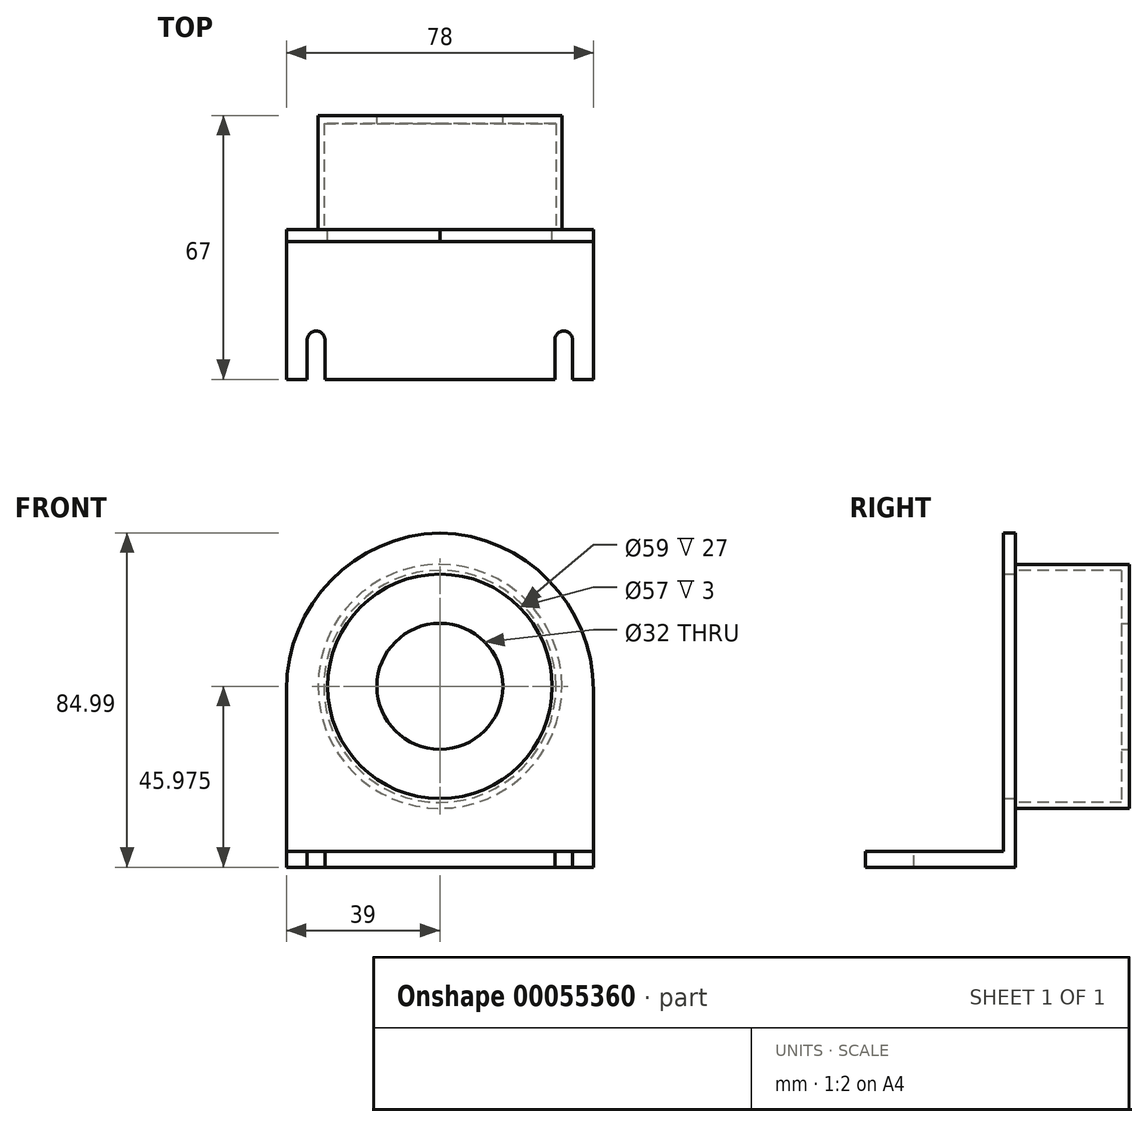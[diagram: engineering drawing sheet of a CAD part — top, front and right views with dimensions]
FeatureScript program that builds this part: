
annotation { "Feature Type Name" : "Feature", "Feature Type Description" : "" }
export const myFeature = defineFeature(function(context is Context, id is Id, definition is map)
    precondition{}
    {
        {
            var Q0;
            Q0=qCreatedBy(makeId("Top.planeOp"),FACE);
            var sketch = newSketch(context, id + "F0", { "sketchPlane" : qUnion([Q0])});
            skLineSegment(sketch, "E0.rect.bottom", {"start": v(39, 19) * mm, "end": v(-39, 19) * mm});
            skLineSegment(sketch, "E0.rect.top", {"start": v(39, -19) * mm, "end": v(-39, -19) * mm});
            skLineSegment(sketch, "E0.rect.left", {"start": v(39, 19) * mm, "end": v(39, -19) * mm});
            skLineSegment(sketch, "E0.rect.right", {"start": v(-39, 19) * mm, "end": v(-39, -19) * mm});
            skPoint(sketch, "E0.rect.middle", {"position": v(0, 0) * mm});
            skSolve(sketch);
        }
        {
            var Q0;
            Q0=qSketchRegion(id+"F0",true);
            extrude(context, id + "F1", {"entities" : qUnion([Q0]), "depth" : 4 * mm});
        }
        {
            var Q0;
            Q0=makeQuery(id+"F1.opExtrude","CAP_FACE",FACE,{"disambiguationData":[OSD([sQuery(id+"F0.wireOp",EDGE,"E0.rect.bottom"),sQuery(id+"F0.wireOp",EDGE,"E0.rect.top"),sQuery(id+"F0.wireOp",EDGE,"E0.rect.left"),sQuery(id+"F0.wireOp",EDGE,"E0.rect.right")])],"isStart":false});
            var sketch = newSketch(context, id + "F2", { "sketchPlane" : qUnion([Q0])});
            skLineSegment(sketch, "E1.bottom", {"start": v(-39, 19) * mm, "end": v(39, 19) * mm});
            skLineSegment(sketch, "E1.top", {"start": v(-39, 16) * mm, "end": v(39, 16) * mm});
            skLineSegment(sketch, "E1.left", {"start": v(-39, 19) * mm, "end": v(-39, 16) * mm});
            skLineSegment(sketch, "E1.right", {"start": v(39, 19) * mm, "end": v(39, 16) * mm});
            skSolve(sketch);
        }
        {
            var Q0;
            Q0=qSketchRegion(id+"F2",true);
            extrude(context, id + "F3", {"entities" : qUnion([Q0]), "operationType" : NewBodyOperationType.ADD, "depth" : 81 * mm});
        }
        {
            var Q0;
            Q0=makeQuery(id+"F3.opExtrude","CAP_EDGE",EDGE,{"disambiguationData":[OSD([sQuery(id+"F2.wireOp",EDGE,"E1.right")])],"isStart":false});
            var Q1;
            Q1=makeQuery(id+"F3.opExtrude","CAP_EDGE",EDGE,{"disambiguationData":[OSD([sQuery(id+"F2.wireOp",EDGE,"E1.left")])],"isStart":false});
            fillet(context, id + "F4", {"entities" : qUnion([Q0, Q1]), "radius" : 40 * mm, "tangentPropagation" : true, "allowEdgeOverflow" : false});
        }
        {
            var Q0;
            Q0=makeQuery(id+"F3.boolean.opBoolean","MERGE",FACE,{"derivedFrom":[makeQuery(id+"F1.opExtrude","SWEPT_FACE",FACE,{"disambiguationData":[OSD([sQuery(id+"F0.wireOp",EDGE,"E0.rect.bottom")])]}),makeQuery(id+"F3.opExtrude","SWEPT_FACE",FACE,{"disambiguationData":[OSD([sQuery(id+"F2.wireOp",EDGE,"E1.bottom")])]})]});
            var sketch = newSketch(context, id + "F5", { "sketchPlane" : qUnion([Q0])});
            skPoint(sketch, "E2.first.point", {"position": v(0, 84.99) * mm});
            skPoint(sketch, "E2.second.point", {"position": v(39, 45) * mm});
            skPoint(sketch, "E2.third.point", {"position": v(-39, 45) * mm});
            skCircle(sketch, "E3", {"center": v(0, 45.98) * mm, "radius": 31 * mm});
            skCircle(sketch, "E4", {"center": v(0, 45.98) * mm, "radius": 29.5 * mm});
            skSolve(sketch);
        }
        {
            var Q0;
            Q0=qSketchRegion(id+"F5",true);
            extrude(context, id + "F6", {"entities" : qUnion([Q0]), "operationType" : NewBodyOperationType.ADD, "depth" : 27 * mm});
        }
        {
            var Q0;
            Q0=makeQuery(id+"F6.boolean.opBoolean","SPLIT",FACE,{"disambiguationData":[TD([makeQuery(id+"F6.opExtrude","SWEPT_FACE",FACE,{"disambiguationData":[OSD([sQuery(id+"F5.wireOp",EDGE,"E4")])]})])],"derivedFrom":makeQuery(id+"F3.boolean.opBoolean","MERGE",FACE,{"derivedFrom":[makeQuery(id+"F1.opExtrude","SWEPT_FACE",FACE,{"disambiguationData":[OSD([sQuery(id+"F0.wireOp",EDGE,"E0.rect.bottom")])]}),makeQuery(id+"F3.opExtrude","SWEPT_FACE",FACE,{"disambiguationData":[OSD([sQuery(id+"F2.wireOp",EDGE,"E1.bottom")])]})]})});
            var sketch = newSketch(context, id + "F7", { "sketchPlane" : qUnion([Q0])});
            skCircle(sketch, "E5", {"center": v(0, 45.98) * mm, "radius": 28.5 * mm});
            skSolve(sketch);
        }
        {
            var Q0;
            Q0=qSketchRegion(id+"F7",true);
            extrude(context, id + "F8", {"entities" : qUnion([Q0]), "operationType" : NewBodyOperationType.REMOVE, "endBound" : BoundingType.UP_TO_NEXT, "oppositeDirection" : true, "depth" : 25 * mm});
        }
        {
            var Q0;
            Q0=makeQuery(id+"F6.opExtrude","CAP_FACE",FACE,{"disambiguationData":[OSD([sQuery(id+"F5.wireOp",EDGE,"E3"),sQuery(id+"F5.wireOp",EDGE,"E4")])],"isStart":false});
            var sketch = newSketch(context, id + "F9", { "sketchPlane" : qUnion([Q0])});
            skCircle(sketch, "E6", {"center": v(0, 45.98) * mm, "radius": 31 * mm});
            skSolve(sketch);
        }
        {
            var Q0;
            Q0=qSketchRegion(id+"F9",true);
            extrude(context, id + "F10", {"entities" : qUnion([Q0]), "operationType" : NewBodyOperationType.ADD, "depth" : 2 * mm});
        }
        {
            var Q0;
            Q0=makeQuery(id+"F10.opExtrude","CAP_FACE",FACE,{"disambiguationData":[OSD([sQuery(id+"F9.wireOp",EDGE,"E6")])],"isStart":false});
            var sketch = newSketch(context, id + "F11", { "sketchPlane" : qUnion([Q0])});
            skCircle(sketch, "E7", {"center": v(0, 45.98) * mm, "radius": 16 * mm});
            skSolve(sketch);
        }
        {
            var Q0;
            Q0=qSketchRegion(id+"F11",true);
            extrude(context, id + "F12", {"entities" : qUnion([Q0]), "operationType" : NewBodyOperationType.REMOVE, "endBound" : BoundingType.UP_TO_NEXT, "oppositeDirection" : true, "depth" : 25 * mm});
        }
        {
            var Q0;
            Q0=makeQuery(id+"F1.opExtrude","CAP_FACE",FACE,{"disambiguationData":[OSD([sQuery(id+"F0.wireOp",EDGE,"E0.rect.bottom"),sQuery(id+"F0.wireOp",EDGE,"E0.rect.top"),sQuery(id+"F0.wireOp",EDGE,"E0.rect.left"),sQuery(id+"F0.wireOp",EDGE,"E0.rect.right")])],"isStart":false});
            var sketch = newSketch(context, id + "F13", { "sketchPlane" : qUnion([Q0])});
            skLineSegment(sketch, "E8", {"start": v(39, -19) * mm, "end": v(33.7, -19) * mm, "construction": true});
            skLineSegment(sketch, "E9.bottom", {"start": v(33.7, -19) * mm, "end": v(29.2, -19) * mm});
            skLineSegment(sketch, "E9.top", {"start": v(33.7, -9) * mm, "end": v(29.2, -9) * mm});
            skLineSegment(sketch, "E9.left", {"start": v(33.7, -19) * mm, "end": v(33.7, -9) * mm});
            skLineSegment(sketch, "E9.right", {"start": v(29.2, -19) * mm, "end": v(29.2, -9) * mm});
            skCircle(sketch, "E10", {"center": v(31.45, -9) * mm, "radius": 2.25 * mm});
            skLineSegment(sketch, "E11", {"start": v(0, -19) * mm, "end": v(0, 59.27) * mm});
            skPoint(sketch, "E11.endSnap0", {"position": v(0, -19) * mm});
            skLineSegment(sketch, "E12.MirrorCS", {"start": v(-33.7, -9) * mm, "end": v(-29.2, -9) * mm});
            skLineSegment(sketch, "E13.MirrorCS", {"start": v(-33.7, -19) * mm, "end": v(-29.2, -19) * mm});
            skLineSegment(sketch, "E14.MirrorCS", {"start": v(-33.7, -19) * mm, "end": v(-33.7, -9) * mm});
            skLineSegment(sketch, "E15.MirrorCS", {"start": v(-29.2, -19) * mm, "end": v(-29.2, -9) * mm});
            skCircle(sketch, "E16.MirrorC", {"center": v(-31.45, -9) * mm, "radius": 2.25 * mm});
            skSolve(sketch);
        }
        {
            var Q0;
            Q0=qSketchRegion(id+"F13",true);
            extrude(context, id + "F14", {"entities" : qUnion([Q0]), "operationType" : NewBodyOperationType.REMOVE, "endBound" : BoundingType.UP_TO_NEXT, "oppositeDirection" : true, "depth" : 25 * mm});
        }
    });
